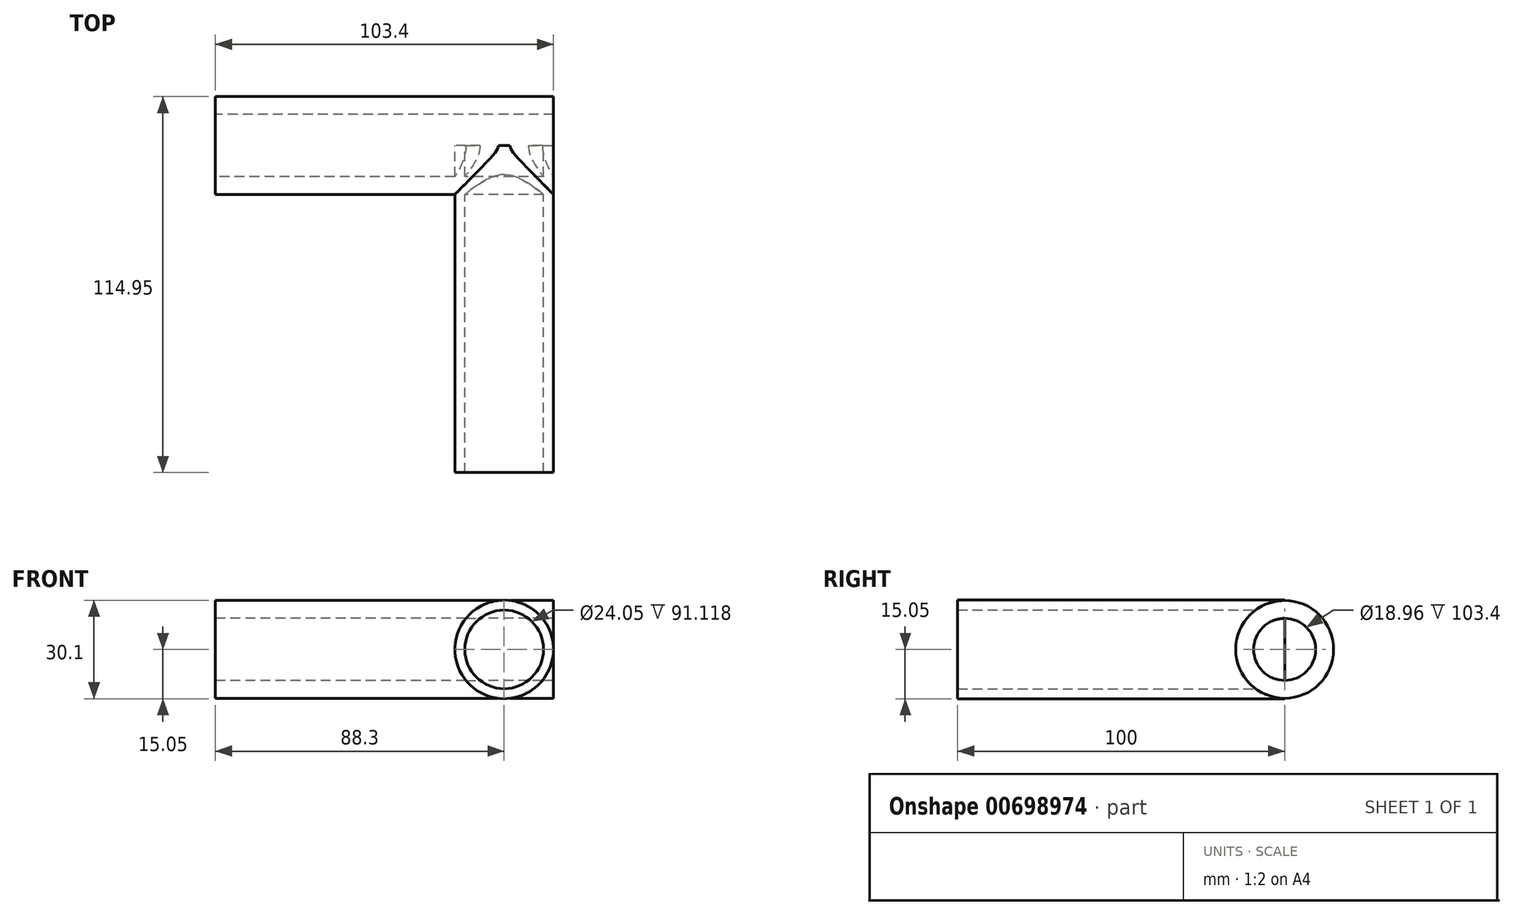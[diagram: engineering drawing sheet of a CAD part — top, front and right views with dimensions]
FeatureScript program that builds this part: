
annotation { "Feature Type Name" : "Feature", "Feature Type Description" : "" }
export const myFeature = defineFeature(function(context is Context, id is Id, definition is map)
    precondition{}
    {
        {
            var Q0;
            Q0=qCreatedBy(makeId("Front.planeOp"),FACE);
            var sketch = newSketch(context, id + "F0", { "sketchPlane" : qUnion([Q0])});
            skCircle(sketch, "E0", {"center": v(0, 0) * mm, "radius": 15.05 * mm});
            skCircle(sketch, "E1", {"center": v(0, 0) * mm, "radius": 12.02 * mm});
            skPoint(sketch, "E2", {"position": v(20.73, 0) * mm});
            skSolve(sketch);
        }
        {
            var Q0;
            Q0=makeQuery(id+"F0.imprint","IMPRINT",FACE,{"disambiguationData":[TD([[makeQuery(id+"F0.imprint","IMPRINT",EDGE,{"derivedFrom":sQuery(id+"F0.wireOp",EDGE,"E0")}),1.0]])]});
            extrude(context, id + "F1", {"entities" : qUnion([Q0]), "depth" : 100 * mm, "offsetDistance" : 25 * mm});
        }
        {
            var Q0;
            Q0=qCreatedBy(makeId("Right.planeOp"),FACE);
            var sketch = newSketch(context, id + "F2", { "sketchPlane" : qUnion([Q0])});
            skCircle(sketch, "E3", {"center": v(0, 0) * mm, "radius": 14.95 * mm});
            skCircle(sketch, "E4", {"center": v(0, 0) * mm, "radius": 9.48 * mm});
            skPoint(sketch, "E5", {"position": v(-9.48, 0) * mm});
            skSolve(sketch);
        }
        {
            var Q0;
            Q0=makeQuery(id+"F2.imprint","IMPRINT",FACE,{"disambiguationData":[TD([[makeQuery(id+"F2.imprint","IMPRINT",EDGE,{"derivedFrom":sQuery(id+"F2.wireOp",EDGE,"E3")}),1.0]])]});
            extrude(context, id + "F3", {"entities" : qUnion([Q0]), "operationType" : NewBodyOperationType.ADD, "depth" : 15.1 * mm, "offsetDistance" : 25 * mm});
        }
        {
            var Q0;
            Q0=makeQuery(id+"F2.imprint","IMPRINT",FACE,{"disambiguationData":[TD([[makeQuery(id+"F2.imprint","IMPRINT",EDGE,{"derivedFrom":sQuery(id+"F2.wireOp",EDGE,"E3")}),1.0]])]});
            extrude(context, id + "F4", {"entities" : qUnion([Q0]), "operationType" : NewBodyOperationType.ADD, "oppositeDirection" : true, "depth" : 88.3 * mm, "offsetDistance" : 25 * mm});
        }
    });
